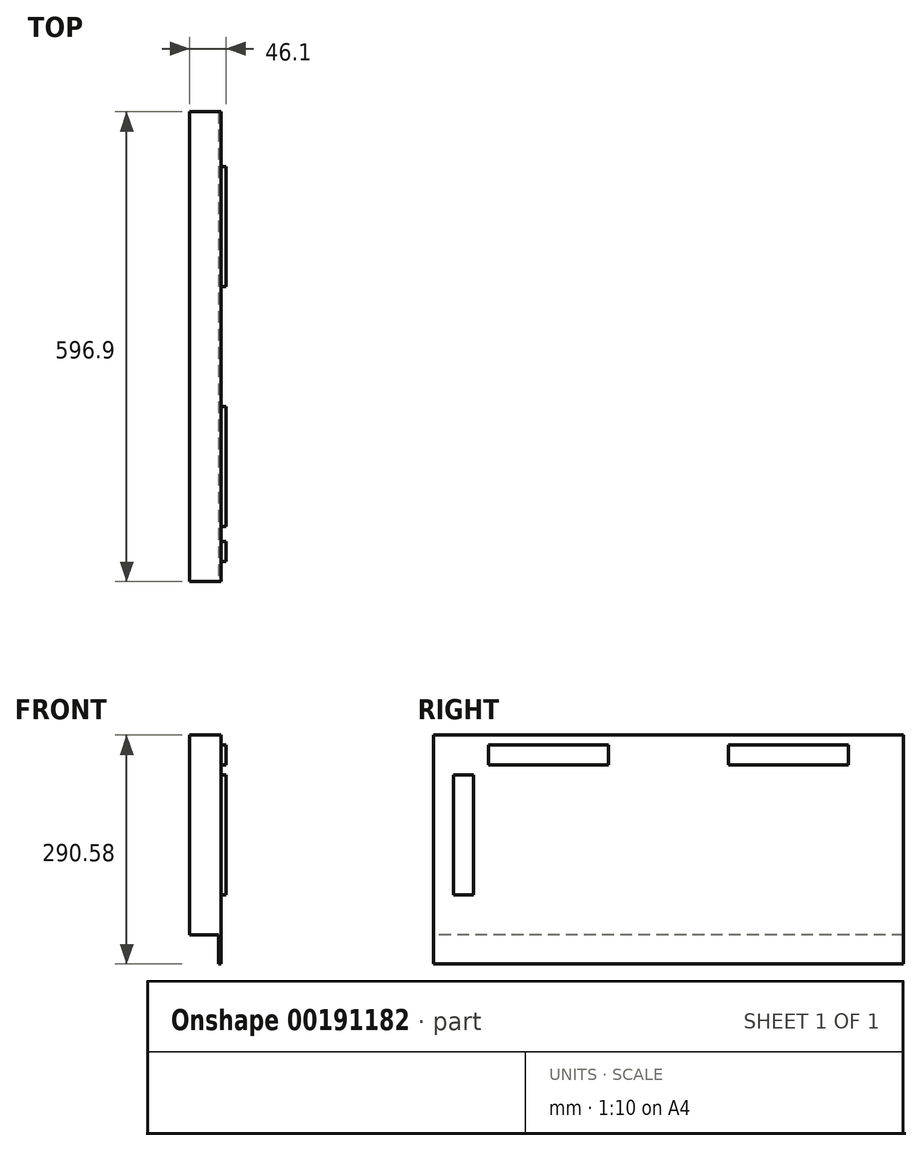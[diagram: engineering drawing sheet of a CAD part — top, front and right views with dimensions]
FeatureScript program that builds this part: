
annotation { "Feature Type Name" : "Feature", "Feature Type Description" : "" }
export const myFeature = defineFeature(function(context is Context, id is Id, definition is map)
    precondition{}
    {
        {
            var Q0;
            Q0=qCreatedBy(makeId("Right.planeOp"),FACE);
            var sketch = newSketch(context, id + "F0", { "sketchPlane" : qUnion([Q0])});
            skLineSegment(sketch, "E0.bottom", {"start": v(298.45, -127) * mm, "end": v(-298.45, -127) * mm});
            skLineSegment(sketch, "E0.top", {"start": v(298.45, 127) * mm, "end": v(-298.45, 127) * mm});
            skLineSegment(sketch, "E0.left", {"start": v(298.45, -127) * mm, "end": v(298.45, 127) * mm});
            skLineSegment(sketch, "E0.right", {"start": v(-298.45, -127) * mm, "end": v(-298.45, 127) * mm});
            skPoint(sketch, "E0.middle", {"position": v(0, 0) * mm});
            skSolve(sketch);
        }
        {
            var Q0;
            Q0=qSketchRegion(id+"F0",true);
            extrude(context, id + "F1", {"entities" : qUnion([Q0]), "depth" : 36.58 * mm});
        }
        {
            var Q0;
            Q0=makeQuery(id+"F1.opExtrude","CAP_FACE",FACE,{"disambiguationData":[OSD([sQuery(id+"F0.wireOp",EDGE,"E0.bottom"),sQuery(id+"F0.wireOp",EDGE,"E0.top"),sQuery(id+"F0.wireOp",EDGE,"E0.left"),sQuery(id+"F0.wireOp",EDGE,"E0.right")])],"isStart":false});
            var sketch = newSketch(context, id + "F2", { "sketchPlane" : qUnion([Q0])});
            skLineSegment(sketch, "E1.bottom", {"start": v(-298.45, 127) * mm, "end": v(298.45, 127) * mm});
            skLineSegment(sketch, "E1.top", {"start": v(-298.45, -163.58) * mm, "end": v(298.45, -163.58) * mm});
            skLineSegment(sketch, "E1.left", {"start": v(-298.45, 127) * mm, "end": v(-298.45, -163.58) * mm});
            skLineSegment(sketch, "E1.right", {"start": v(298.45, 127) * mm, "end": v(298.45, -163.58) * mm});
            skSolve(sketch);
        }
        {
            var Q0;
            Q0 = qSketchRegion(id + "F2", true);
            extrude(context, id + "F3", {"entities" : qUnion([Q0]), "operationType" : NewBodyOperationType.ADD, "depth" : 3.17 * mm});
        }
        {
            var Q0;
            Q0=makeQuery(id+"F3.opExtrude","CAP_FACE",FACE,{"disambiguationData":[OSD([sQuery(id+"F2.wireOp",EDGE,"E1.bottom"),sQuery(id+"F2.wireOp",EDGE,"E1.top"),sQuery(id+"F2.wireOp",EDGE,"E1.left"),sQuery(id+"F2.wireOp",EDGE,"E1.right")])],"isStart":false});
            var sketch = newSketch(context, id + "F4", { "sketchPlane" : qUnion([Q0])});
            skLineSegment(sketch, "E2", {"start": v(0, 235.2) * mm, "end": v(0, -302.02) * mm, "construction": true});
            skLineSegment(sketch, "E3.bottom", {"start": v(228.6, 114.3) * mm, "end": v(76.2, 114.3) * mm});
            skLineSegment(sketch, "E3.top", {"start": v(228.6, 88.9) * mm, "end": v(76.2, 88.9) * mm});
            skLineSegment(sketch, "E3.left", {"start": v(228.6, 114.3) * mm, "end": v(228.6, 88.9) * mm});
            skLineSegment(sketch, "E3.right", {"start": v(76.2, 114.3) * mm, "end": v(76.2, 88.9) * mm});
            skLineSegment(sketch, "E4.bottom", {"start": v(-247.65, -76.2) * mm, "end": v(-273.05, -76.2) * mm});
            skLineSegment(sketch, "E4.top", {"start": v(-247.65, 76.2) * mm, "end": v(-273.05, 76.2) * mm});
            skLineSegment(sketch, "E4.left", {"start": v(-247.65, -76.2) * mm, "end": v(-247.65, 76.2) * mm});
            skLineSegment(sketch, "E4.right", {"start": v(-273.05, -76.2) * mm, "end": v(-273.05, 76.2) * mm});
            skPoint(sketch, "E4.middle", {"position": v(-260.35, 0) * mm});
            skLineSegment(sketch, "E5.MirrorCS", {"start": v(-76.2, 114.3) * mm, "end": v(-76.2, 88.9) * mm});
            skLineSegment(sketch, "E6.MirrorCS", {"start": v(-228.6, 114.3) * mm, "end": v(-76.2, 114.3) * mm});
            skLineSegment(sketch, "E7.MirrorCS", {"start": v(-228.6, 88.9) * mm, "end": v(-76.2, 88.9) * mm});
            skLineSegment(sketch, "E8.MirrorCS", {"start": v(-228.6, 114.3) * mm, "end": v(-228.6, 88.9) * mm});
            skSolve(sketch);
        }
        {
            var Q0;
            Q0 = qSketchRegion(id + "F4", true);
            extrude(context, id + "F5", {"entities" : qUnion([Q0]), "operationType" : NewBodyOperationType.ADD, "depth" : 6.35 * mm});
        }
    });
